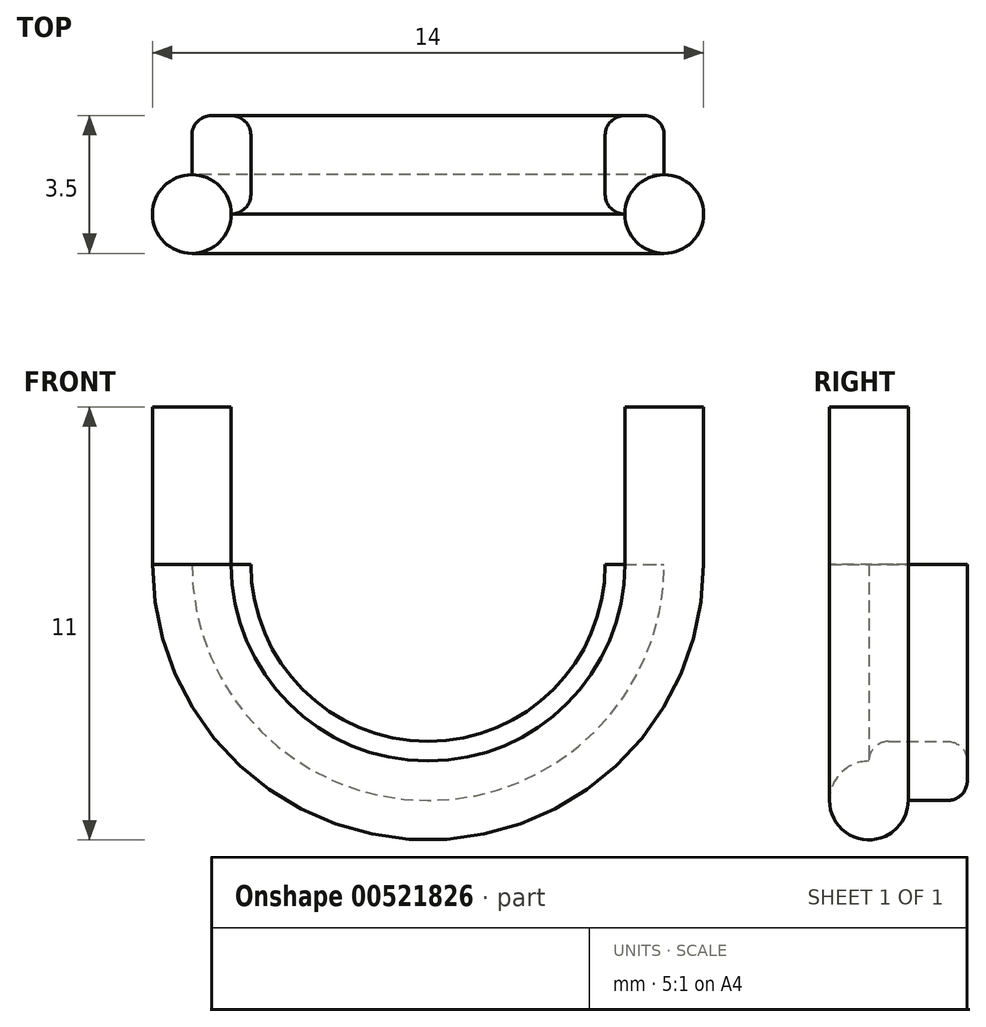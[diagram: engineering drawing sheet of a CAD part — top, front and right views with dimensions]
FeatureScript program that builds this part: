
annotation { "Feature Type Name" : "Feature", "Feature Type Description" : "" }
export const myFeature = defineFeature(function(context is Context, id is Id, definition is map)
    precondition{}
    {
        {
            var Q0;
            Q0=qCreatedBy(makeId("Top.planeOp"),FACE);
            var sketch = newSketch(context, id + "F0", { "sketchPlane" : qUnion([Q0])});
            skLineSegment(sketch, "E0.bottom", {"start": v(4.5, 2.5) * mm, "end": v(-4.5, 2.5) * mm});
            skLineSegment(sketch, "E0.top", {"start": v(4.5, -2.5) * mm, "end": v(-4.5, -2.5) * mm});
            skLineSegment(sketch, "E0.left", {"start": v(4.5, 2.5) * mm, "end": v(4.5, -2.5) * mm});
            skLineSegment(sketch, "E0.right", {"start": v(-4.5, 2.5) * mm, "end": v(-4.5, -2.5) * mm});
            skPoint(sketch, "E0.middle", {"position": v(0, 0) * mm});
            skLineSegment(sketch, "E1.bottom", {"start": v(4.5, 2.5) * mm, "end": v(7.5, 2.5) * mm});
            skLineSegment(sketch, "E1.top", {"start": v(4.5, -2.5) * mm, "end": v(7.5, -2.5) * mm});
            skLineSegment(sketch, "E1.right", {"start": v(7.5, 2.5) * mm, "end": v(7.5, -2.5) * mm});
            skLineSegment(sketch, "E2.bottom", {"start": v(-4.5, 2.5) * mm, "end": v(-7.5, 2.5) * mm});
            skLineSegment(sketch, "E2.top", {"start": v(-4.5, -2.5) * mm, "end": v(-7.5, -2.5) * mm});
            skLineSegment(sketch, "E2.right", {"start": v(-7.5, 2.5) * mm, "end": v(-7.5, -2.5) * mm});
            skLineSegment(sketch, "E3", {"start": v(0, 2.5) * mm, "end": v(0, -2.5) * mm});
            skLineSegment(sketch, "E4.bottom", {"start": v(-4.5, 2.5) * mm, "end": v(-6, 2.5) * mm});
            skLineSegment(sketch, "E4.top", {"start": v(-4.5, 0) * mm, "end": v(-6, 0) * mm});
            skLineSegment(sketch, "E4.left", {"start": v(-4.5, 2.5) * mm, "end": v(-4.5, 0) * mm});
            skLineSegment(sketch, "E4.right", {"start": v(-6, 2.5) * mm, "end": v(-6, 0) * mm});
            skLineSegment(sketch, "E5.bottom", {"start": v(4.5, 2.5) * mm, "end": v(6, 2.5) * mm});
            skLineSegment(sketch, "E5.top", {"start": v(4.5, 0) * mm, "end": v(6, 0) * mm});
            skLineSegment(sketch, "E5.left", {"start": v(4.5, 2.5) * mm, "end": v(4.5, 0) * mm});
            skLineSegment(sketch, "E5.right", {"start": v(6, 2.5) * mm, "end": v(6, 0) * mm});
            skCircle(sketch, "E6", {"center": v(-6, 0) * mm, "radius": 1 * mm});
            skCircle(sketch, "E7", {"center": v(6, 0) * mm, "radius": 1 * mm});
            skSolve(sketch);
        }
        {
            var Q0;
            Q0=makeQuery(id+"F0.imprint","IMPRINT",FACE,{"disambiguationData":[TD([[makeQuery(id+"F0.imprint","IMPRINT",EDGE,{"derivedFrom":sQuery(id+"F0.wireOp",EDGE,"E2.bottom")}),1.0]])]});
            var Q1;
            {var subQ1=sQuery(id+"F0.wireOp",EDGE,"E4.bottom");Q1=makeQuery(id+"F0.imprint","IMPRINT",FACE,{"disambiguationData":[TD([[makeQuery(id+"F0.imprint","IMPRINT",EDGE,{"derivedFrom":subQ1}),1.0]])]});}
            var Q2;
            {var subQ0=sQuery(id+"F0.wireOp",EDGE,"E4.right");var subQ1=sQuery(id+"F0.wireOp",EDGE,"E4.top");var subQ2=makeQuery(id+"F0.imprint","INTERSECT",VERTEX,{"derivedFrom":[subQ1,subQ0]});Q2=makeQuery(id+"F0.imprint","IMPRINT",FACE,{"disambiguationData":[TD([[makeQuery(id+"F0.imprint","IMPRINT",EDGE,{"disambiguationData":[TD([[subQ2,1.0]])],"derivedFrom":subQ1}),1.0]])]});}
            var Q3;
            {var subQ0=sQuery(id+"F0.wireOp",EDGE,"E4.right");var subQ1=sQuery(id+"F0.wireOp",EDGE,"E4.top");var subQ2=makeQuery(id+"F0.imprint","INTERSECT",VERTEX,{"derivedFrom":[subQ1,subQ0]});Q3=makeQuery(id+"F0.imprint","IMPRINT",FACE,{"disambiguationData":[TD([[makeQuery(id+"F0.imprint","IMPRINT",EDGE,{"disambiguationData":[TD([[subQ2,1.0]])],"derivedFrom":subQ1}),-1.0]])]});}
            var Q4;
            Q4=sQuery(id+"F0.wireOp",EDGE,"E3");
            revolve(context, id + "F1", {"entities" : qUnion([Q0, Q1, Q2, Q3]), "axis" : qUnion([Q4]), "revolveType" : RevolveType.ONE_DIRECTION, "angle" : 180 * degree});
        }
        {
            var Q0;
            Q0=makeQuery(id+"F1.opRevolve","SWEPT_EDGE",EDGE,{"disambiguationData":[OSD([sQuery(id+"F0.wireOp",EDGE,"E2.bottom"),sQuery(id+"F0.wireOp",EDGE,"E2.right")])]});
            var Q1;
            Q1=makeQuery(id+"F1.opRevolve","SWEPT_EDGE",EDGE,{"disambiguationData":[OSD([sQuery(id+"F0.wireOp",EDGE,"E2.top"),sQuery(id+"F0.wireOp",EDGE,"E2.right")])]});
            var Q2;
            Q2=makeQuery(id+"F1.opRevolve","SWEPT_EDGE",EDGE,{"disambiguationData":[OSD([sQuery(id+"F0.wireOp",EDGE,"E0.top"),sQuery(id+"F0.wireOp",EDGE,"E2.top"),sQuery(id+"F0.wireOp",EDGE,"E0.right")])]});
            var Q3;
            Q3=makeQuery(id+"F1.opRevolve","SWEPT_EDGE",EDGE,{"disambiguationData":[OSD([sQuery(id+"F0.wireOp",EDGE,"E0.bottom"),sQuery(id+"F0.wireOp",EDGE,"E4.bottom"),sQuery(id+"F0.wireOp",EDGE,"E4.left")])]});
            fillet(context, id + "F2", {"entities" : qUnion([Q0, Q1, Q2, Q3]), "radius" : .5 * mm, "tangentPropagation" : true, "allowEdgeOverflow" : false});
        }
        {
            var Q0;
            {var subQ0=sQuery(id+"F0.wireOp",EDGE,"E4.right");var subQ1=sQuery(id+"F0.wireOp",EDGE,"E4.top");var subQ2=makeQuery(id+"F0.imprint","INTERSECT",VERTEX,{"derivedFrom":[subQ1,subQ0]});Q0=makeQuery(id+"F0.imprint","IMPRINT",FACE,{"disambiguationData":[TD([[makeQuery(id+"F0.imprint","IMPRINT",EDGE,{"disambiguationData":[TD([[subQ2,1.0]])],"derivedFrom":subQ1}),1.0]])]});}
            var Q1;
            {var subQ0=sQuery(id+"F0.wireOp",EDGE,"E4.right");var subQ1=sQuery(id+"F0.wireOp",EDGE,"E4.top");var subQ2=makeQuery(id+"F0.imprint","INTERSECT",VERTEX,{"derivedFrom":[subQ1,subQ0]});Q1=makeQuery(id+"F0.imprint","IMPRINT",FACE,{"disambiguationData":[TD([[makeQuery(id+"F0.imprint","IMPRINT",EDGE,{"disambiguationData":[TD([[subQ2,1.0]])],"derivedFrom":subQ1}),-1.0]])]});}
            extrude(context, id + "F3", {"entities" : qUnion([Q0, Q1]), "depth" : 4 * mm, "offsetDistance" : 25 * mm});
        }
        {
            var Q0;
            Q0=makeQuery(id+"F1.opRevolve","CAP_FACE",FACE,{"disambiguationData":[OSD([sQuery(id+"F0.wireOp",EDGE,"E2.bottom"),sQuery(id+"F0.wireOp",EDGE,"E2.top"),sQuery(id+"F0.wireOp",EDGE,"E0.right"),sQuery(id+"F0.wireOp",EDGE,"E2.right"),sQuery(id+"F0.wireOp",EDGE,"E4.bottom"),sQuery(id+"F0.wireOp",EDGE,"E4.left")])],"isStart":false});
            var sketch = newSketch(context, id + "F4", { "sketchPlane" : qUnion([Q0])});
            skLineSegment(sketch, "E8.bottom", {"start": v(4.5, 2.5) * mm, "end": v(-4.5, 2.5) * mm});
            skLineSegment(sketch, "E8.top", {"start": v(4.5, -2.5) * mm, "end": v(-4.5, -2.5) * mm});
            skLineSegment(sketch, "E8.left", {"start": v(4.5, 2.5) * mm, "end": v(4.5, -2.5) * mm});
            skLineSegment(sketch, "E8.right", {"start": v(-4.5, 2.5) * mm, "end": v(-4.5, -2.5) * mm});
            skPoint(sketch, "E8.middle", {"position": v(0, 0) * mm});
            skLineSegment(sketch, "E9.bottom", {"start": v(4.5, 2.5) * mm, "end": v(7.5, 2.5) * mm});
            skLineSegment(sketch, "E9.top", {"start": v(4.5, -2.5) * mm, "end": v(7.5, -2.5) * mm});
            skLineSegment(sketch, "E9.right", {"start": v(7.5, 2.5) * mm, "end": v(7.5, -2.5) * mm});
            skLineSegment(sketch, "E10.bottom", {"start": v(-4.5, 2.5) * mm, "end": v(-7.5, 2.5) * mm});
            skLineSegment(sketch, "E10.top", {"start": v(-4.5, -2.5) * mm, "end": v(-7.5, -2.5) * mm});
            skLineSegment(sketch, "E10.right", {"start": v(-7.5, 2.5) * mm, "end": v(-7.5, -2.5) * mm});
            skLineSegment(sketch, "E11", {"start": v(0, 2.5) * mm, "end": v(0, -2.5) * mm});
            skLineSegment(sketch, "E12.bottom", {"start": v(-4.5, 2.5) * mm, "end": v(-6, 2.5) * mm});
            skLineSegment(sketch, "E12.top", {"start": v(-4.5, 0) * mm, "end": v(-6, 0) * mm});
            skLineSegment(sketch, "E12.left", {"start": v(-4.5, 2.5) * mm, "end": v(-4.5, 0) * mm});
            skLineSegment(sketch, "E12.right", {"start": v(-6, 2.5) * mm, "end": v(-6, 0) * mm});
            skLineSegment(sketch, "E13.bottom", {"start": v(4.5, 2.5) * mm, "end": v(6, 2.5) * mm});
            skLineSegment(sketch, "E13.top", {"start": v(4.5, 0) * mm, "end": v(6, 0) * mm});
            skLineSegment(sketch, "E13.left", {"start": v(4.5, 2.5) * mm, "end": v(4.5, 0) * mm});
            skLineSegment(sketch, "E13.right", {"start": v(6, 2.5) * mm, "end": v(6, 0) * mm});
            skCircle(sketch, "E14", {"center": v(-6, 0) * mm, "radius": 1 * mm});
            skCircle(sketch, "E15", {"center": v(6, 0) * mm, "radius": 1 * mm});
            skSolve(sketch);
        }
        {
            var Q0;
            {var subQ0=sQuery(id+"F4.wireOp",EDGE,"E13.right");var subQ1=sQuery(id+"F4.wireOp",EDGE,"E13.top");var subQ2=makeQuery(id+"F4.imprint","INTERSECT",VERTEX,{"derivedFrom":[subQ1,subQ0]});Q0=makeQuery(id+"F4.imprint","IMPRINT",FACE,{"disambiguationData":[TD([[makeQuery(id+"F4.imprint","IMPRINT",EDGE,{"disambiguationData":[TD([[subQ2,1.0]])],"derivedFrom":subQ1}),-1.0]])]});}
            var Q1;
            {var subQ0=sQuery(id+"F4.wireOp",EDGE,"E13.right");var subQ1=sQuery(id+"F4.wireOp",EDGE,"E13.top");var subQ2=makeQuery(id+"F4.imprint","INTERSECT",VERTEX,{"derivedFrom":[subQ1,subQ0]});Q1=makeQuery(id+"F4.imprint","IMPRINT",FACE,{"disambiguationData":[TD([[makeQuery(id+"F4.imprint","IMPRINT",EDGE,{"disambiguationData":[TD([[subQ2,1.0]])],"derivedFrom":subQ1}),1.0]])]});}
            extrude(context, id + "F5", {"entities" : qUnion([Q0, Q1]), "operationType" : NewBodyOperationType.ADD, "depth" : 4 * mm, "offsetDistance" : 25 * mm});
        }
    });
